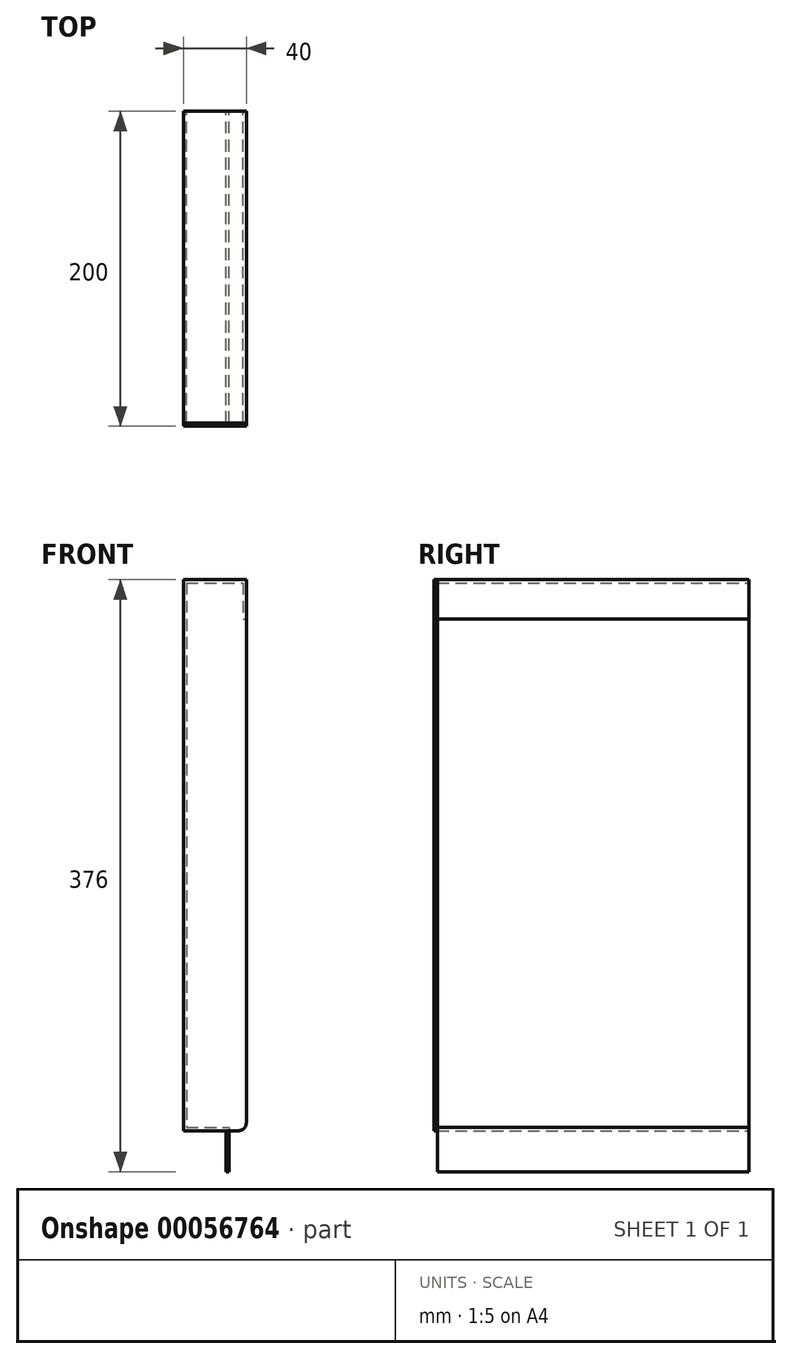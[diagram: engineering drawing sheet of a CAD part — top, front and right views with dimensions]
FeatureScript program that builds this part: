
annotation { "Feature Type Name" : "Feature", "Feature Type Description" : "" }
export const myFeature = defineFeature(function(context is Context, id is Id, definition is map)
    precondition{}
    {
        {
            var Q0;
            Q0=qCreatedBy(makeId("Front.planeOp"),FACE);
            var sketch = newSketch(context, id + "F0", { "sketchPlane" : qUnion([Q0])});
            skLineSegment(sketch, "E0", {"start": v(0, 0) * mm, "end": v(0, -350) * mm});
            skLineSegment(sketch, "E1", {"start": v(0, -350) * mm, "end": v(27, -350) * mm});
            skLineSegment(sketch, "E2", {"start": v(27, -350) * mm, "end": v(27, -376) * mm});
            skLineSegment(sketch, "E3", {"start": v(0, 0) * mm, "end": v(40, 0) * mm});
            skLineSegment(sketch, "E4", {"start": v(40, 0) * mm, "end": v(40, -25) * mm});
            skLineSegment(sketch, "E5.0", {"start": v(38, -2) * mm, "end": v(38, -25) * mm});
            skLineSegment(sketch, "E5.1", {"start": v(29, -348) * mm, "end": v(29, -376) * mm});
            skLineSegment(sketch, "E5.2", {"start": v(2, -348) * mm, "end": v(29, -348) * mm});
            skLineSegment(sketch, "E5.3", {"start": v(2, -2) * mm, "end": v(2, -348) * mm});
            skLineSegment(sketch, "E5.4", {"start": v(2, -2) * mm, "end": v(38, -2) * mm});
            skLineSegment(sketch, "E6", {"start": v(38, -25) * mm, "end": v(40, -25) * mm});
            skLineSegment(sketch, "E7", {"start": v(27, -376) * mm, "end": v(29, -376) * mm});
            skSolve(sketch);
        }
        {
            var Q0;
            Q0=qCreatedBy(makeId("Top.planeOp"),FACE);
            var sketch = newSketch(context, id + "F1", { "sketchPlane" : qUnion([Q0])});
            skLineSegment(sketch, "E8", {"start": v(0, 0) * mm, "end": v(0, 198) * mm});
            skSolve(sketch);
        }
        {
            var Q0;
            Q0=qSketchRegion(id+"F0",true);
            var Q1;
            Q1=qConstructionFilter(qBodyType(qCreatedBy(id+"F1",EDGE),BodyType.WIRE),ConstructionObject.NO);
            sweep(context, id + "F2", {"profiles" : qUnion([Q0]), "path" : qUnion([Q1])});
        }
        {
            var Q0;
            Q0=makeQuery(id+"F2.opSweep","CAP_FACE",FACE,{"disambiguationData":[OSD([sQuery(id+"F0.wireOp",EDGE,"E0"),sQuery(id+"F0.wireOp",EDGE,"E1"),sQuery(id+"F0.wireOp",EDGE,"E2"),sQuery(id+"F0.wireOp",EDGE,"E3"),sQuery(id+"F0.wireOp",EDGE,"E4"),sQuery(id+"F0.wireOp",EDGE,"E5.0"),sQuery(id+"F0.wireOp",EDGE,"E5.1"),sQuery(id+"F0.wireOp",EDGE,"E5.2"),sQuery(id+"F0.wireOp",EDGE,"E5.3"),sQuery(id+"F0.wireOp",EDGE,"E5.4"),sQuery(id+"F0.wireOp",EDGE,"E6"),sQuery(id+"F0.wireOp",EDGE,"E7"),sQuery(id+"F1.wireOp",VERTEX,"E8.start")])],"isStart":true});
            var sketch = newSketch(context, id + "F3", { "sketchPlane" : qUnion([Q0])});
            skLineSegment(sketch, "E9.0", {"start": v(40, 0) * mm, "end": v(0, 0) * mm});
            skLineSegment(sketch, "E10.0", {"start": v(0, -350) * mm, "end": v(0, 0) * mm});
            skPoint(sketch, "E11.0.end.orphan", {"position": v(27, -350) * mm});
            skPoint(sketch, "E12.0.start.orphan", {"position": v(40, -25) * mm});
            skLineSegment(sketch, "E13", {"start": v(40, 0) * mm, "end": v(40, -345) * mm});
            skLineSegment(sketch, "E14", {"start": v(35, -350) * mm, "end": v(0, -350) * mm});
            skPoint(sketch, "E15.visualSharp", {"position": v(40, -350) * mm});
            skArc(sketch, "E15.filletArc", {"start": v(35, -350) * mm, "mid": v(38.54, -348.54) * mm, "end": v(40, -345) * mm});
            skSolve(sketch);
        }
        {
            var Q0;
            Q0=qSketchRegion(id+"F3",true);
            extrude(context, id + "F4", {"entities" : qUnion([Q0]), "depth" : 2 * mm});
        }
    });
